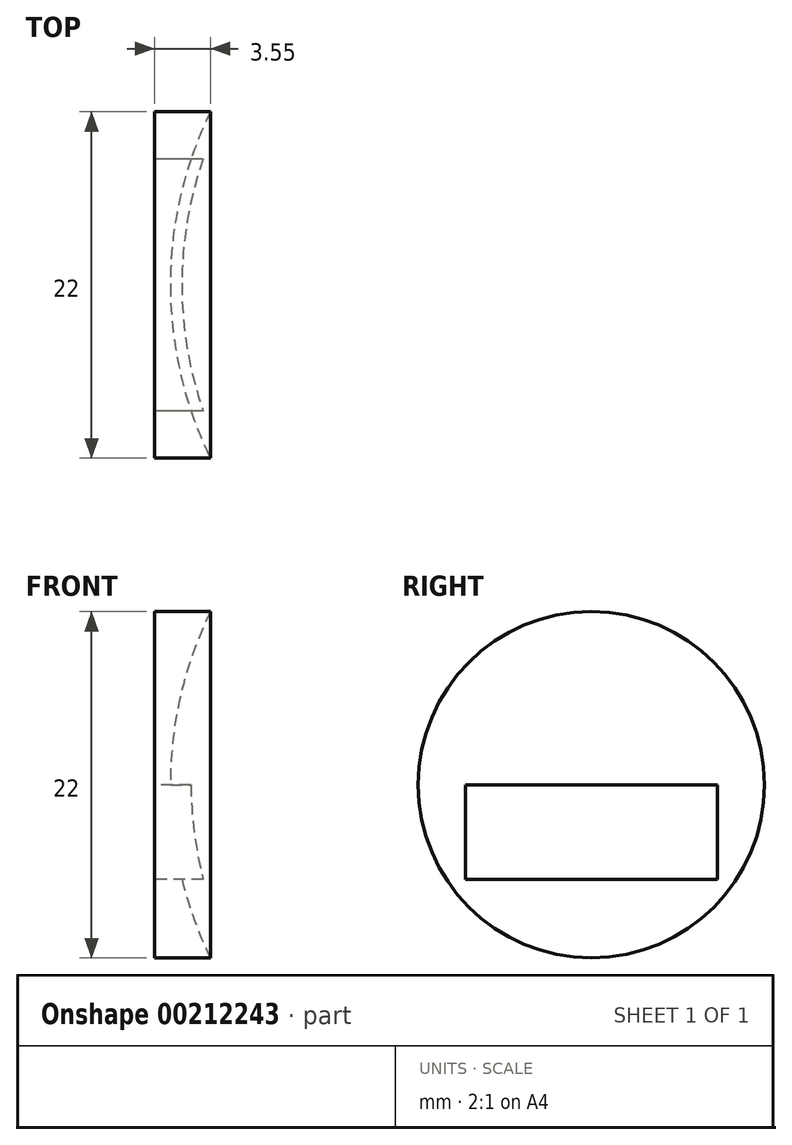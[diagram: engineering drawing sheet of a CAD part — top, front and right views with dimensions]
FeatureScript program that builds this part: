
annotation { "Feature Type Name" : "Feature", "Feature Type Description" : "" }
export const myFeature = defineFeature(function(context is Context, id is Id, definition is map)
    precondition{}
    {
        {
            var Q0;
            Q0=qCreatedBy(makeId("Front.planeOp"),FACE);
            var sketch = newSketch(context, id + "F0", { "sketchPlane" : qUnion([Q0])});
            skLineSegment(sketch, "E0", {"start": v(0, 11) * mm, "end": v(0, -11) * mm});
            skLineSegment(sketch, "E1", {"start": v(-10.39, 0) * mm, "end": v(26, 0) * mm, "construction": true});
            skArc(sketch, "E2", {"start": v(3.55, 11) * mm, "mid": v(1, 0) * mm, "end": v(3.55, -11) * mm});
            skLineSegment(sketch, "E3", {"start": v(0, 11) * mm, "end": v(3.55, 11) * mm});
            skLineSegment(sketch, "E4", {"start": v(0, -11) * mm, "end": v(3.55, -11) * mm});
            skLineSegment(sketch, "E5", {"start": v(0, 0) * mm, "end": v(1, 0) * mm});
            skSolve(sketch);
        }
        {
            var Q0;
            {var subQ0=sQuery(id+"F0.wireOp",EDGE,"E3");Q0=makeQuery(id+"F0.imprint","IMPRINT",FACE,{"disambiguationData":[TD([[makeQuery(id+"F0.imprint","IMPRINT",EDGE,{"derivedFrom":subQ0}),-1.0]])]});}
            var Q1;
            Q1=sQuery(id+"F0.wireOp",EDGE,"E5");
            revolve(context, id + "F1", {"entities" : qUnion([Q0]), "axis" : qUnion([Q1]), "revolveType" : RevolveType.FULL});
        }
        {
            var Q0;
            Q0=makeQuery(id+"F1.opRevolve","SWEPT_FACE",FACE,{"disambiguationData":[OSD([sQuery(id+"F0.wireOp",EDGE,"E0")])]});
            var sketch = newSketch(context, id + "F2", { "sketchPlane" : qUnion([Q0])});
            skLineSegment(sketch, "E6.bottom", {"start": v(-8, 0) * mm, "end": v(8, 0) * mm});
            skLineSegment(sketch, "E6.top", {"start": v(-8, -6) * mm, "end": v(8, -6) * mm});
            skLineSegment(sketch, "E6.left", {"start": v(-8, 0) * mm, "end": v(-8, -6) * mm});
            skLineSegment(sketch, "E6.right", {"start": v(8, 0) * mm, "end": v(8, -6) * mm});
            skLineSegment(sketch, "E7", {"start": v(0, 11) * mm, "end": v(0, -11) * mm, "construction": true});
            skSolve(sketch);
        }
        {
            var Q0;
            Q0 = qSketchRegion(id + "F2", true);
            extrude(context, id + "F3", {"entities" : qUnion([Q0]), "operationType" : NewBodyOperationType.REMOVE, "endBound" : BoundingType.THROUGH_ALL, "oppositeDirection" : true, "depth" : 10 * mm});
        }
    });
